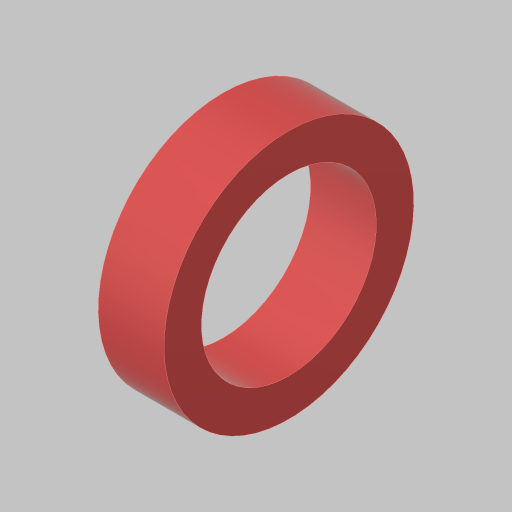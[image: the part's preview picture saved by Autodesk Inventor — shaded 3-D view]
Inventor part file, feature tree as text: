
AUTODESK INVENTOR PART (.ipt)
format: ipt  version: 2023.5 (Build 275446000, 446)  size: 114,688 bytes
history: native  units: in
note: dims shown in document units (in); Inventor stores cm internally (conversion verified against a paired STEP export)
features: extrude x1, sketch x1
ambient origin geometry x8: Origin, YZ Plane, XZ Plane, XY Plane, X Axis, Y Axis, Z Axis, Center Point
bodies: Solid1 (feature_tree)
feature tree (2):
  extrude  "Extrusion1"  Depth=0.22in
  sketch  "Sketch1"  dims[d0=0.585in d1=0.125in d2=0.22in d3=0.0in]
